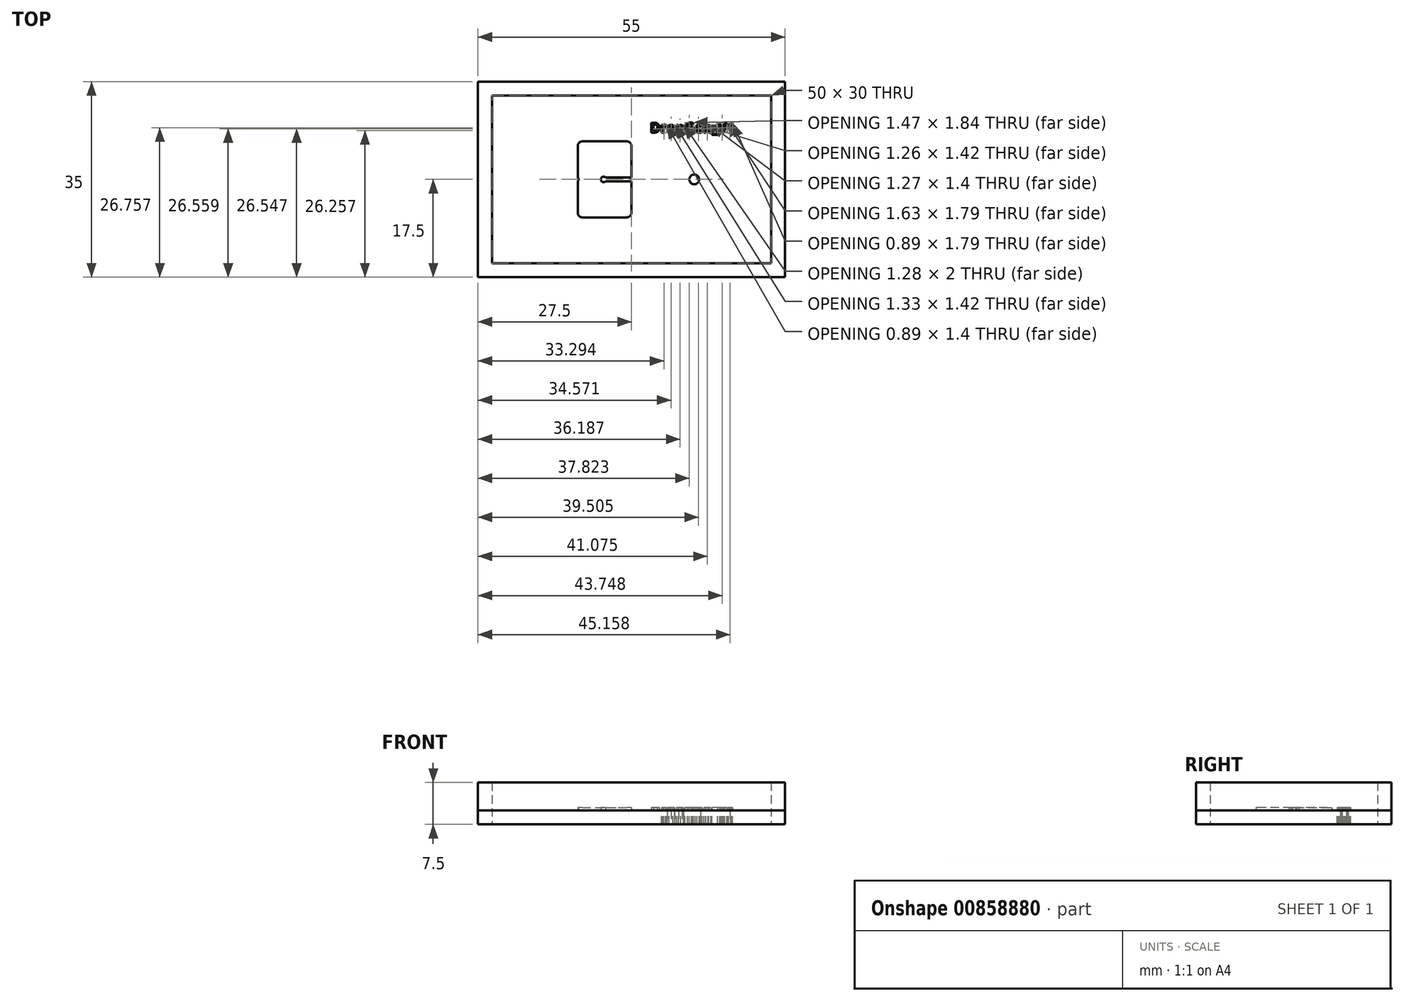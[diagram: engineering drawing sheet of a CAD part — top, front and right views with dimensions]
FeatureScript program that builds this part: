
annotation { "Feature Type Name" : "Feature", "Feature Type Description" : "" }
export const myFeature = defineFeature(function(context is Context, id is Id, definition is map)
    precondition{}
    {
        {
            var Q0;
            Q0=qCreatedBy(makeId("Top.planeOp"),FACE);
            var sketch = newSketch(context, id + "F0", { "sketchPlane" : qUnion([Q0])});
            skLineSegment(sketch, "E0.bottom", {"start": v(25, 15) * mm, "end": v(-25, 15) * mm});
            skLineSegment(sketch, "E0.top", {"start": v(25, -15) * mm, "end": v(-25, -15) * mm});
            skLineSegment(sketch, "E0.left", {"start": v(25, 15) * mm, "end": v(25, -15) * mm});
            skLineSegment(sketch, "E0.right", {"start": v(-25, 15) * mm, "end": v(-25, -15) * mm});
            skPoint(sketch, "E0.middle", {"position": v(0, 0) * mm});
            skLineSegment(sketch, "E1", {"start": v(-25, 0) * mm, "end": v(25, 0) * mm, "construction": true});
            skCircle(sketch, "E2", {"center": v(-10, 0) * mm, "radius": 0.5 * mm, "construction": true});
            skCircle(sketch, "E3", {"center": v(-10, 0) * mm, "radius": 0.38 * mm, "construction": true});
            skLineSegment(sketch, "E4", {"start": v(-9.62, 0) * mm, "end": v(-9.62, 6) * mm, "construction": true});
            skLineSegment(sketch, "E5", {"start": v(-10.37, 0) * mm, "end": v(-10.37, 6) * mm, "construction": true});
            skLineSegment(sketch, "E6", {"start": v(-9.62, 0) * mm, "end": v(-9.62, -6) * mm, "construction": true});
            skLineSegment(sketch, "E7", {"start": v(-10.37, 0) * mm, "end": v(-10.37, -6) * mm, "construction": true});
            skLineSegment(sketch, "E8", {"start": v(-9.62, 6) * mm, "end": v(-8.82, 6) * mm, "construction": true});
            skLineSegment(sketch, "E9", {"start": v(-8.82, 6) * mm, "end": v(-8.82, 6.8) * mm, "construction": true});
            skArc(sketch, "E10", {"start": v(-9.62, 6) * mm, "mid": v(-9.4, 6.57) * mm, "end": v(-8.82, 6.8) * mm});
            skArc(sketch, "E11", {"start": v(-10.37, 6) * mm, "mid": v(-9.92, 7.1) * mm, "end": v(-8.82, 7.55) * mm});
            skLineSegment(sketch, "E12", {"start": v(-8.82, 6.8) * mm, "end": v(-0.82, 6.8) * mm});
            skLineSegment(sketch, "E13", {"start": v(-8.82, 7.55) * mm, "end": v(-0.82, 7.55) * mm});
            skLineSegment(sketch, "E14", {"start": v(-0.82, 6.8) * mm, "end": v(-0.82, 6) * mm, "construction": true});
            skLineSegment(sketch, "E15", {"start": v(-0.82, 6) * mm, "end": v(-0.02, 6) * mm, "construction": true});
            skArc(sketch, "E16", {"start": v(-0.82, 6.8) * mm, "mid": v(-0.26, 6.57) * mm, "end": v(-0.02, 6) * mm});
            skArc(sketch, "E17", {"start": v(-0.82, 7.55) * mm, "mid": v(0.27, 7.1) * mm, "end": v(0.73, 6) * mm});
            skLineSegment(sketch, "E18.MirrorCS", {"start": v(-8.82, -7.55) * mm, "end": v(-0.82, -7.55) * mm});
            skLineSegment(sketch, "E19.MirrorCS", {"start": v(-8.82, -6.8) * mm, "end": v(-0.82, -6.8) * mm});
            skArc(sketch, "E20.MirrorCS", {"start": v(-10.37, -6) * mm, "mid": v(-9.92, -7.1) * mm, "end": v(-8.82, -7.55) * mm});
            skArc(sketch, "E21.MirrorCS", {"start": v(-9.62, -6) * mm, "mid": v(-9.4, -6.57) * mm, "end": v(-8.82, -6.8) * mm});
            skArc(sketch, "E22.MirrorCS", {"start": v(-0.82, -6.8) * mm, "mid": v(-0.26, -6.57) * mm, "end": v(-0.02, -6) * mm});
            skArc(sketch, "E23.MirrorCS", {"start": v(-0.82, -7.55) * mm, "mid": v(0.27, -7.1) * mm, "end": v(0.73, -6) * mm});
            skLineSegment(sketch, "E24", {"start": v(-0.02, 6) * mm, "end": v(-0.02, 0) * mm, "construction": true});
            skCircle(sketch, "E25", {"center": v(-5, 0) * mm, "radius": 0.5 * mm, "construction": true});
            skCircle(sketch, "E26", {"center": v(-5, 0) * mm, "radius": 0.38 * mm, "construction": true});
            skLineSegment(sketch, "E27", {"start": v(-5, 0) * mm, "end": v(-5, 0.38) * mm, "construction": true});
            skLineSegment(sketch, "E28", {"start": v(-5, 0) * mm, "end": v(-5, -0.38) * mm, "construction": true});
            skLineSegment(sketch, "E29", {"start": v(-5, 0.38) * mm, "end": v(-0.02, 0.38) * mm, "construction": true});
            skLineSegment(sketch, "E30.MirrorCS", {"start": v(-5, -0.38) * mm, "end": v(-0.02, -0.38) * mm, "construction": true});
            skLineSegment(sketch, "E31", {"start": v(-0.02, 6) * mm, "end": v(-0.02, 0.38) * mm});
            skLineSegment(sketch, "E32", {"start": v(-0.02, -0.38) * mm, "end": v(-0.02, -6) * mm});
            skLineSegment(sketch, "E33", {"start": v(0.73, 6) * mm, "end": v(0.73, 0.38) * mm});
            skLineSegment(sketch, "E34", {"start": v(0.73, -6) * mm, "end": v(0.73, -0.38) * mm});
            skLineSegment(sketch, "E35", {"start": v(0.73, 0.38) * mm, "end": v(1.23, 0.38) * mm, "construction": true});
            skLineSegment(sketch, "E36", {"start": v(0.73, 0.38) * mm, "end": v(1.23, 0.87) * mm});
            skLineSegment(sketch, "E37.MirrorCS", {"start": v(0.73, -0.38) * mm, "end": v(1.23, -0.87) * mm});
            skLineSegment(sketch, "E38", {"start": v(1.23, -0.87) * mm, "end": v(11.23, -0.87) * mm});
            skLineSegment(sketch, "E39.MirrorCS", {"start": v(1.23, 0.87) * mm, "end": v(11.23, 0.87) * mm});
            skLineSegment(sketch, "E40", {"start": v(11.23, 0.87) * mm, "end": v(11.23, -0.87) * mm, "construction": true});
            skCircle(sketch, "E41", {"center": v(11.23, 0) * mm, "radius": 0.87 * mm});
            skLineSegment(sketch, "E42.bottom", {"start": v(27.5, -17.5) * mm, "end": v(-27.5, -17.5) * mm});
            skLineSegment(sketch, "E42.top", {"start": v(27.5, 17.5) * mm, "end": v(-27.5, 17.5) * mm});
            skLineSegment(sketch, "E42.left", {"start": v(27.5, -17.5) * mm, "end": v(27.5, 17.5) * mm});
            skLineSegment(sketch, "E42.right", {"start": v(-27.5, -17.5) * mm, "end": v(-27.5, 17.5) * mm});
            skLineSegment(sketch, "E43", {"start": v(-4.67, -0.38) * mm, "end": v(-0.02, -0.38) * mm});
            skLineSegment(sketch, "E44.MirrorCS", {"start": v(-4.67, 0.38) * mm, "end": v(-0.02, 0.38) * mm});
            skArc(sketch, "E45", {"start": v(-4.67, 0.38) * mm, "mid": v(-5.5, 0) * mm, "end": v(-4.67, -0.38) * mm});
            skArc(sketch, "E46", {"start": v(-10.37, -0.33) * mm, "mid": v(-10.5, 0) * mm, "end": v(-10.37, 0.33) * mm});
            skArc(sketch, "E47", {"start": v(-9.62, -0.33) * mm, "mid": v(-9.5, 0) * mm, "end": v(-9.62, 0.33) * mm});
            skLineSegment(sketch, "E48", {"start": v(-9.62, 0.33) * mm, "end": v(-9.62, 6) * mm});
            skLineSegment(sketch, "E49", {"start": v(-10.37, 0.33) * mm, "end": v(-10.37, 6) * mm});
            skLineSegment(sketch, "E50", {"start": v(-9.62, -0.33) * mm, "end": v(-9.62, -6) * mm});
            skLineSegment(sketch, "E51", {"start": v(-10.37, -0.33) * mm, "end": v(-10.37, -6) * mm});
            skText(sketch, "E52", { "text": "DropGen_V1", "fontName": "OpenSans-Bold.ttf"});
            const initialGuessF0  = {"E52": [0.00329, 0.00836, 1, 0, 0.00181]};
            skSetInitialGuess(sketch, initialGuessF0);
            skSolve(sketch);
        }
        {
            var Q0;
            Q0=makeQuery(id+"F0.imprint","IMPRINT",FACE,{"disambiguationData":[TD([[makeQuery(id+"F0.imprint","IMPRINT",EDGE,{"derivedFrom":sQuery(id+"F0.wireOp",EDGE,"E0.bottom")}),-1.0]])]});
            extrude(context, id + "F1", {"entities" : qUnion([Q0]), "depth" : 5 * mm, "offsetDistance" : 25 * mm});
        }
        {
            var Q0;
            Q0 = qSketchRegion(id + "F0", true);
            extrude(context, id + "F2", {"entities" : qUnion([Q0]), "operationType" : NewBodyOperationType.ADD, "oppositeDirection" : true, "depth" : 2.5 * mm, "offsetDistance" : 25 * mm});
        }
        {
            var Q0;
            Q0=makeQuery(id+"F0.imprint","IMPRINT",FACE,{"disambiguationData":[TD([[makeQuery(id+"F0.imprint","IMPRINT",EDGE,{"derivedFrom":sQuery(id+"F0.wireOp",EDGE,"E10")}),1.0]])]});
            var Q1;
            {var subQ0=sQuery(id+"F0.wireOp",EDGE,"E41");var subQ1=makeQuery(id+"F0.imprint","INTERSECT",VERTEX,{"derivedFrom":[sQuery(id+"F0.wireOp",EDGE,"E38"),subQ0]});Q1=makeQuery(id+"F0.imprint","IMPRINT",FACE,{"disambiguationData":[TD([[makeQuery(id+"F0.imprint","IMPRINT",EDGE,{"disambiguationData":[TD([[subQ1,1.0]])],"derivedFrom":subQ0}),1.0]])]});}
            extrude(context, id + "F3", {"entities" : qUnion([Q0, Q1]), "operationType" : NewBodyOperationType.ADD, "depth" : 0.5 * mm, "offsetDistance" : 25 * mm});
        }
        {
            var Q0;
            Q0=makeQuery(id+"F0.imprint","IMPRINT",FACE,{"disambiguationData":[TD([[makeQuery(id+"F0.imprint","IMPRINT",EDGE,{"derivedFrom":sQuery(id+"F0.wireOp",EDGE,"E52.sketch_text.stroke-0")}),-1.0]])]});
            var Q1;
            Q1=makeQuery(id+"F0.imprint","IMPRINT",FACE,{"disambiguationData":[TD([[makeQuery(id+"F0.imprint","IMPRINT",EDGE,{"derivedFrom":sQuery(id+"F0.wireOp",EDGE,"E52.sketch_text.stroke-12")}),-1.0]])]});
            var Q2;
            Q2=makeQuery(id+"F0.imprint","IMPRINT",FACE,{"disambiguationData":[TD([[makeQuery(id+"F0.imprint","IMPRINT",EDGE,{"derivedFrom":sQuery(id+"F0.wireOp",EDGE,"E52.sketch_text.stroke-25")}),-1.0]])]});
            var Q3;
            Q3=makeQuery(id+"F0.imprint","IMPRINT",FACE,{"disambiguationData":[TD([[makeQuery(id+"F0.imprint","IMPRINT",EDGE,{"derivedFrom":sQuery(id+"F0.wireOp",EDGE,"E52.sketch_text.stroke-43")}),-1.0]])]});
            var Q4;
            Q4=makeQuery(id+"F0.imprint","IMPRINT",FACE,{"disambiguationData":[TD([[makeQuery(id+"F0.imprint","IMPRINT",EDGE,{"derivedFrom":sQuery(id+"F0.wireOp",EDGE,"E52.sketch_text.stroke-66")}),-1.0]])]});
            var Q5;
            Q5=makeQuery(id+"F0.imprint","IMPRINT",FACE,{"disambiguationData":[TD([[makeQuery(id+"F0.imprint","IMPRINT",EDGE,{"derivedFrom":sQuery(id+"F0.wireOp",EDGE,"E52.sketch_text.stroke-85")}),-1.0]])]});
            var Q6;
            Q6=makeQuery(id+"F0.imprint","IMPRINT",FACE,{"disambiguationData":[TD([[makeQuery(id+"F0.imprint","IMPRINT",EDGE,{"derivedFrom":sQuery(id+"F0.wireOp",EDGE,"E52.sketch_text.stroke-105")}),-1.0]])]});
            var Q7;
            Q7=makeQuery(id+"F0.imprint","IMPRINT",FACE,{"disambiguationData":[TD([[makeQuery(id+"F0.imprint","IMPRINT",EDGE,{"derivedFrom":sQuery(id+"F0.wireOp",EDGE,"E52.sketch_text.stroke-122")}),-1.0]])]});
            var Q8;
            Q8=makeQuery(id+"F0.imprint","IMPRINT",FACE,{"disambiguationData":[TD([[makeQuery(id+"F0.imprint","IMPRINT",EDGE,{"derivedFrom":sQuery(id+"F0.wireOp",EDGE,"E52.sketch_text.stroke-126")}),-1.0]])]});
            var Q9;
            Q9=makeQuery(id+"F0.imprint","IMPRINT",FACE,{"disambiguationData":[TD([[makeQuery(id+"F0.imprint","IMPRINT",EDGE,{"derivedFrom":sQuery(id+"F0.wireOp",EDGE,"E52.sketch_text.stroke-136")}),-1.0]])]});
            extrude(context, id + "F4", {"entities" : qUnion([Q0, Q1, Q2, Q3, Q4, Q5, Q6, Q7, Q8, Q9]), "depth" : 0.5 * mm, "offsetDistance" : 25 * mm});
        }
        {
            var Q0;
            Q0=makeQuery(id+"F0.imprint","IMPRINT",FACE,{"disambiguationData":[TD([[makeQuery(id+"F0.imprint","IMPRINT",EDGE,{"derivedFrom":sQuery(id+"F0.wireOp",EDGE,"E0.bottom")}),-1.0]])]});
            var Q1;
            Q1=makeQuery(id+"F0.imprint","IMPRINT",FACE,{"disambiguationData":[TD([[makeQuery(id+"F0.imprint","IMPRINT",EDGE,{"derivedFrom":sQuery(id+"F0.wireOp",EDGE,"E0.bottom")}),1.0]])]});
            var Q2;
            Q2=makeQuery(id+"F0.imprint","IMPRINT",FACE,{"disambiguationData":[TD([[makeQuery(id+"F0.imprint","IMPRINT",EDGE,{"derivedFrom":sQuery(id+"F0.wireOp",EDGE,"E10")}),1.0]])]});
            var Q3;
            Q3=makeQuery(id+"F0.imprint","IMPRINT",FACE,{"disambiguationData":[TD([[makeQuery(id+"F0.imprint","IMPRINT",EDGE,{"derivedFrom":sQuery(id+"F0.wireOp",EDGE,"E10")}),-1.0]])]});
            var Q4;
            {var subQ0=sQuery(id+"F0.wireOp",EDGE,"E41");var subQ1=makeQuery(id+"F0.imprint","INTERSECT",VERTEX,{"derivedFrom":[sQuery(id+"F0.wireOp",EDGE,"E38"),subQ0]});Q4=makeQuery(id+"F0.imprint","IMPRINT",FACE,{"disambiguationData":[TD([[makeQuery(id+"F0.imprint","IMPRINT",EDGE,{"disambiguationData":[TD([[subQ1,1.0]])],"derivedFrom":subQ0}),1.0]])]});}
            var Q5;
            Q5=makeQuery(id+"F0.imprint","IMPRINT",FACE,{"disambiguationData":[TD([[makeQuery(id+"F0.imprint","IMPRINT",EDGE,{"derivedFrom":sQuery(id+"F0.wireOp",EDGE,"E52.sketch_text.stroke-7")}),1.0]])]});
            var Q6;
            Q6=makeQuery(id+"F0.imprint","IMPRINT",FACE,{"disambiguationData":[TD([[makeQuery(id+"F0.imprint","IMPRINT",EDGE,{"derivedFrom":sQuery(id+"F0.wireOp",EDGE,"E52.sketch_text.stroke-0")}),-1.0]])]});
            var Q7;
            Q7 = qSketchRegion(id + "F0", true);
            extrude(context, id + "F5", {"entities" : qUnion([Q0, Q1, Q2, Q3, Q4, Q5, Q6, Q7]), "oppositeDirection" : true, "depth" : 2.5 * mm, "offsetDistance" : 25 * mm});
        }
    });
